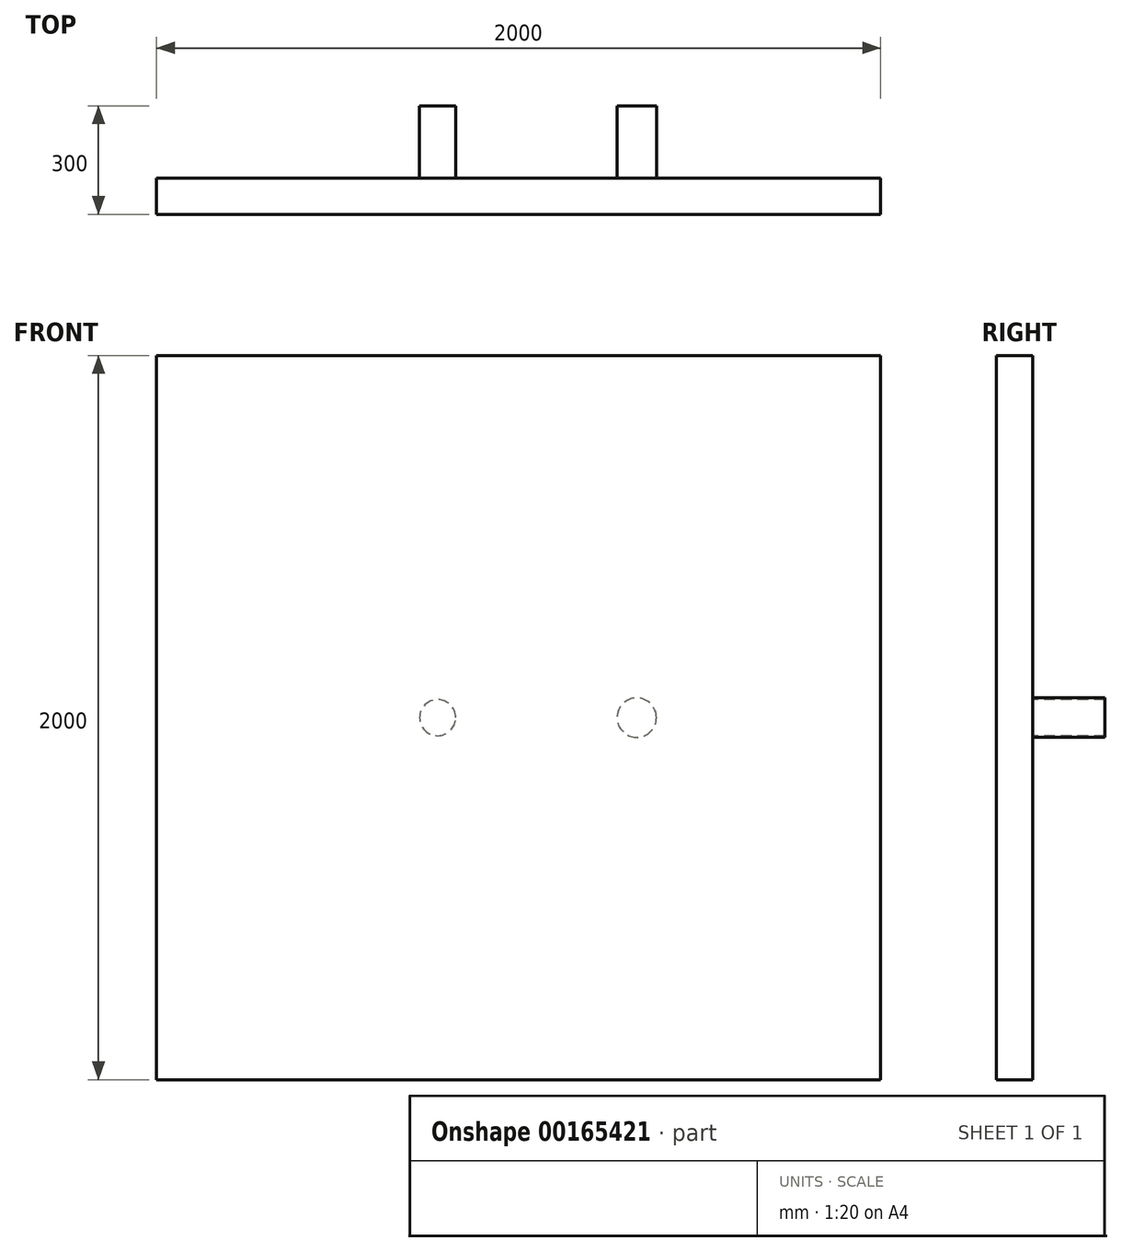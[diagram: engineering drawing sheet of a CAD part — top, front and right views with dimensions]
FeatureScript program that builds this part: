
annotation { "Feature Type Name" : "Feature", "Feature Type Description" : "" }
export const myFeature = defineFeature(function(context is Context, id is Id, definition is map)
    precondition{}
    {
        {
            var Q0;
            Q0=qCreatedBy(makeId("Front.planeOp"),FACE);
            var sketch = newSketch(context, id + "F0", { "sketchPlane" : qUnion([Q0])});
            skLineSegment(sketch, "E0.bottom", {"start": v(-1008.94, 1483.27) * mm, "end": v(991.06, 1483.27) * mm});
            skLineSegment(sketch, "E0.top", {"start": v(-1008.94, -516.73) * mm, "end": v(991.06, -516.73) * mm});
            skLineSegment(sketch, "E0.left", {"start": v(-1008.94, 1483.27) * mm, "end": v(-1008.94, -516.73) * mm});
            skLineSegment(sketch, "E0.right", {"start": v(991.06, 1483.27) * mm, "end": v(991.06, -516.73) * mm});
            skSolve(sketch);
        }
        {
            var Q0;
            Q0=makeQuery(id+"F0.imprint","IMPRINT",FACE,{"disambiguationData":[TD([[makeQuery(id+"F0.imprint","IMPRINT",EDGE,{"derivedFrom":sQuery(id+"F0.wireOp",EDGE,"E0.bottom")}),-1.0]])]});
            extrude(context, id + "F1", {"entities" : qUnion([Q0]), "depth" : 100 * mm});
        }
        {
            var Q0;
            Q0=makeQuery(id+"F1.opExtrude","CAP_FACE",FACE,{"disambiguationData":[OSD([sQuery(id+"F0.wireOp",EDGE,"E0.bottom"),sQuery(id+"F0.wireOp",EDGE,"E0.top"),sQuery(id+"F0.wireOp",EDGE,"E0.left"),sQuery(id+"F0.wireOp",EDGE,"E0.right")])],"isStart":false});
            var sketch = newSketch(context, id + "F2", { "sketchPlane" : qUnion([Q0])});
            skCircle(sketch, "E1", {"center": v(-232.2, 483.27) * mm, "radius": 50 * mm});
            skCircle(sketch, "E2", {"center": v(317.8, 483.27) * mm, "radius": 54.25 * mm});
            skSolve(sketch);
        }
        {
            var Q0;
            Q0=qSketchRegion(id+"F2",true);
            extrude(context, id + "F3", {"entities" : qUnion([Q0]), "operationType" : NewBodyOperationType.ADD, "oppositeDirection" : true, "depth" : 300 * mm});
        }
    });
